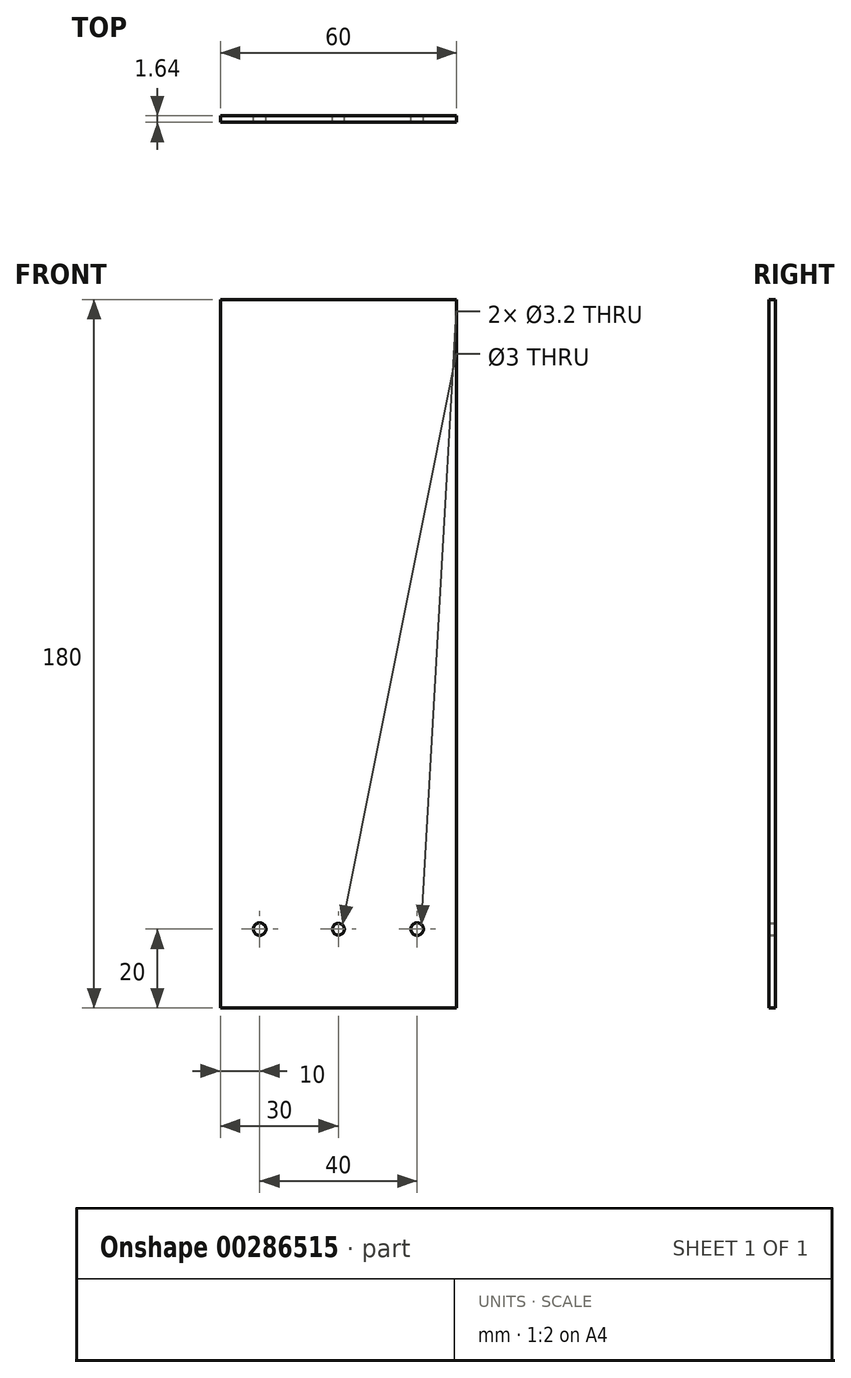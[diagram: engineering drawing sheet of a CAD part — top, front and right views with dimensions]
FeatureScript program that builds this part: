
annotation { "Feature Type Name" : "Feature", "Feature Type Description" : "" }
export const myFeature = defineFeature(function(context is Context, id is Id, definition is map)
    precondition{}
    {
        {
            var Q0;
            Q0=qCreatedBy(makeId("Front.planeOp"),FACE);
            var sketch = newSketch(context, id + "F0", { "sketchPlane" : qUnion([Q0])});
            skLineSegment(sketch, "E0.bottom", {"start": v(30, 183) * mm, "end": v(-30, 183) * mm});
            skLineSegment(sketch, "E0.top", {"start": v(30, 3) * mm, "end": v(-30, 3) * mm});
            skLineSegment(sketch, "E0.left", {"start": v(30, 183) * mm, "end": v(30, 3) * mm});
            skLineSegment(sketch, "E0.right", {"start": v(-30, 183) * mm, "end": v(-30, 3) * mm});
            skPoint(sketch, "E0.middle", {"position": v(0, 93) * mm});
            skCircle(sketch, "E1", {"center": v(-20, 23) * mm, "radius": 1.6 * mm});
            skCircle(sketch, "E2.MirrorC", {"center": v(20, 23) * mm, "radius": 1.6 * mm});
            skCircle(sketch, "E3", {"center": v(0, 23) * mm, "radius": 1.5 * mm});
            skSolve(sketch);
        }
        {
            var Q0;
            Q0=makeQuery(id+"F0.imprint","IMPRINT",FACE,{"disambiguationData":[TD([[makeQuery(id+"F0.imprint","IMPRINT",EDGE,{"derivedFrom":sQuery(id+"F0.wireOp",EDGE,"E0.bottom")}),1.0]])]});
            extrude(context, id + "F1", {"entities" : qUnion([Q0]), "depth" : 1.63 * mm, "offsetDistance" : 25 * mm, "symmetric" : true});
        }
    });
